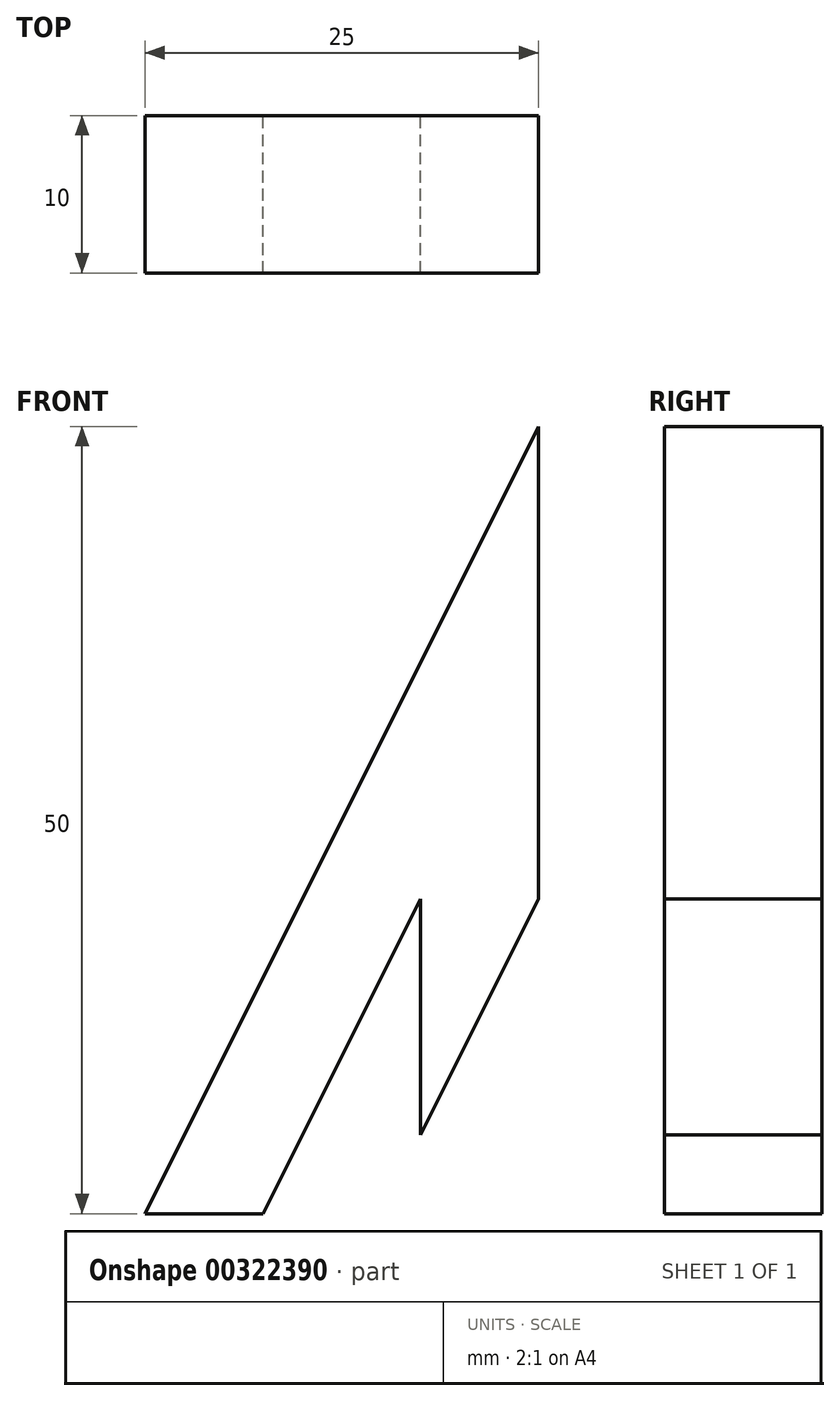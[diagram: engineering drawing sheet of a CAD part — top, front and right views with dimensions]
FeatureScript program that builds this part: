
annotation { "Feature Type Name" : "Feature", "Feature Type Description" : "" }
export const myFeature = defineFeature(function(context is Context, id is Id, definition is map)
    precondition{}
    {
        {
            var Q0;
            Q0=qCreatedBy(makeId("Front.planeOp"),FACE);
            var sketch = newSketch(context, id + "F0", { "sketchPlane" : qUnion([Q0])});
            skLineSegment(sketch, "E0", {"start": v(0, 50) * mm, "end": v(-25, 0) * mm});
            skLineSegment(sketch, "E1", {"start": v(-25, 0) * mm, "end": v(0, 0) * mm});
            skLineSegment(sketch, "E2", {"start": v(0, 0) * mm, "end": v(0, 50) * mm});
            skLineSegment(sketch, "E3", {"start": v(-7.5, 20) * mm, "end": v(-17.5, 0) * mm});
            skLineSegment(sketch, "E4", {"start": v(-17.5, 0) * mm, "end": v(-7.5, 20) * mm});
            skLineSegment(sketch, "E5", {"start": v(-7.5, 20) * mm, "end": v(-7.5, 0) * mm});
            skLineSegment(sketch, "E6", {"start": v(-7.5, 0) * mm, "end": v(-17.5, 0) * mm});
            skLineSegment(sketch, "E7", {"start": v(-7.5, 5) * mm, "end": v(0, 20) * mm});
            skSolve(sketch);
        }
        {
            var Q0;
            {var subQ1=sQuery(id+"F0.wireOp",EDGE,"E0");Q0=makeQuery(id+"F0.imprint","IMPRINT",FACE,{"disambiguationData":[TD([[makeQuery(id+"F0.imprint","IMPRINT",EDGE,{"derivedFrom":subQ1}),1.0]])]});}
            extrude(context, id + "F1", {"entities" : qUnion([Q0]), "depth" : 10 * mm});
        }
    });
